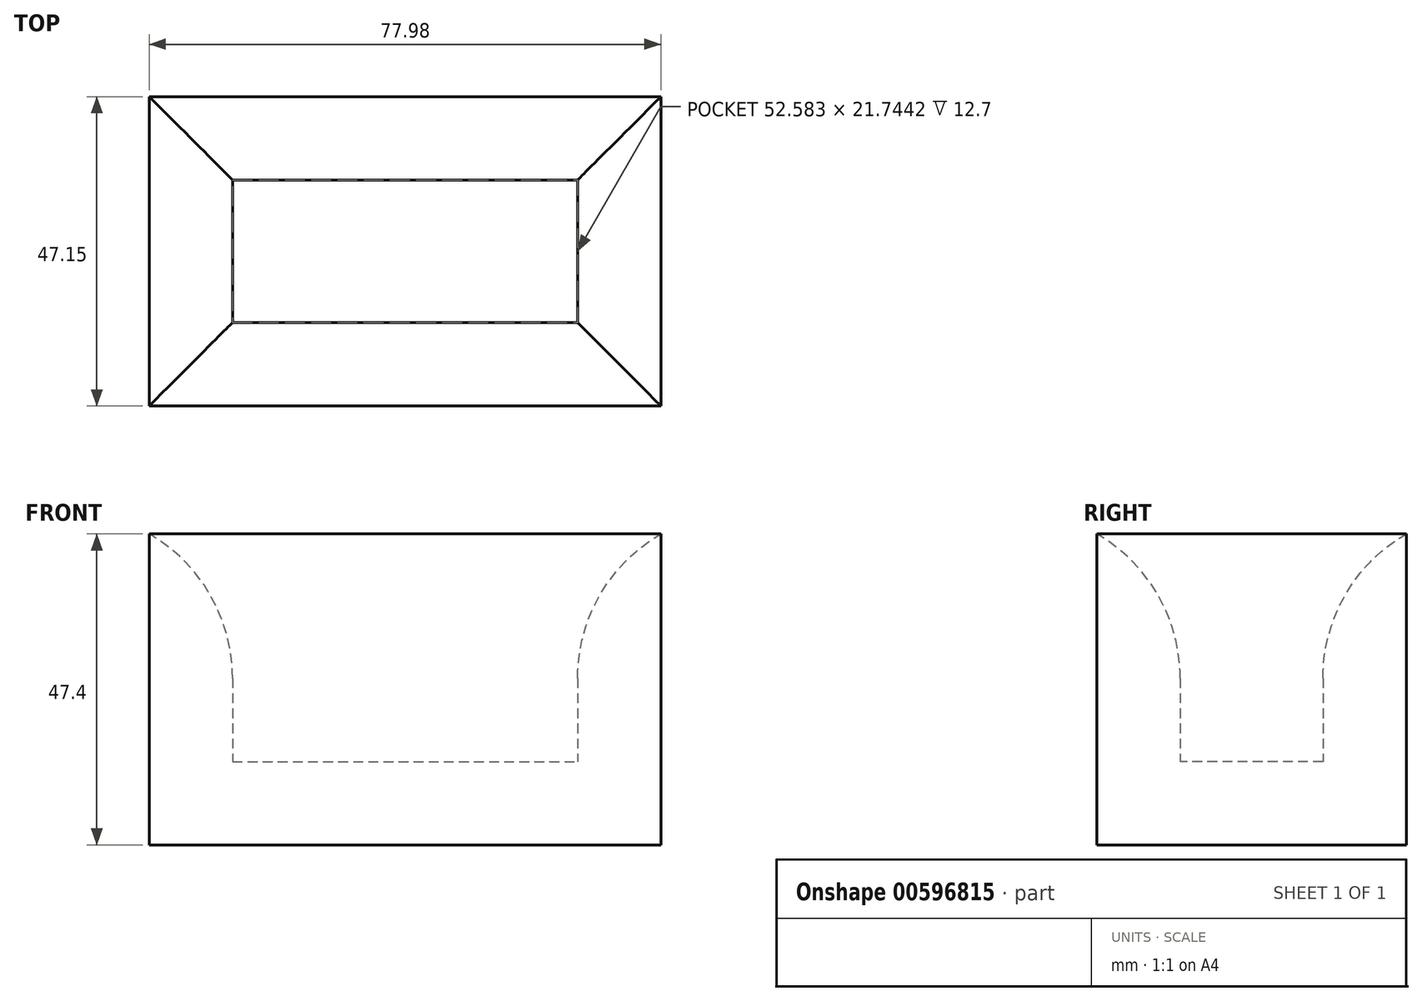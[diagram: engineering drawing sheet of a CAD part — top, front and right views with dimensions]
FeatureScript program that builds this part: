
annotation { "Feature Type Name" : "Feature", "Feature Type Description" : "" }
export const myFeature = defineFeature(function(context is Context, id is Id, definition is map)
    precondition{}
    {
        {
            var Q0;
            Q0=qCreatedBy(makeId("Top.planeOp"),FACE);
            var sketch = newSketch(context, id + "F0", { "sketchPlane" : qUnion([Q0])});
            skLineSegment(sketch, "E0.bottom", {"start": v(-13, 23.46) * mm, "end": v(64.98, 23.46) * mm});
            skLineSegment(sketch, "E0.top", {"start": v(-13, -23.69) * mm, "end": v(64.98, -23.69) * mm});
            skLineSegment(sketch, "E0.left", {"start": v(-13, 23.46) * mm, "end": v(-13, -23.69) * mm});
            skLineSegment(sketch, "E0.right", {"start": v(64.98, 23.46) * mm, "end": v(64.98, -23.69) * mm});
            skSolve(sketch);
        }
        {
            var Q0;
            Q0 = qSketchRegion(id + "F0", true);
            extrude(context, id + "F1", {"entities" : qUnion([Q0]), "depth" : 50.8 * mm, "offsetDistance" : 25.4 * mm});
        }
        {
            var Q0;
            Q0=makeQuery(id+"F1.opExtrude","CAP_FACE",FACE,{"disambiguationData":[OSD([sQuery(id+"F0.wireOp",EDGE,"E0.bottom"),sQuery(id+"F0.wireOp",EDGE,"E0.top"),sQuery(id+"F0.wireOp",EDGE,"E0.left"),sQuery(id+"F0.wireOp",EDGE,"E0.right")])],"isStart":false});
            shell(context, id + "F2", {"entities" : qUnion([Q0]), "thickness" : 12.7 * mm});
        }
        {
            var Q0;
            {var subQ0=sQuery(id+"F0.wireOp",EDGE,"E0.bottom");Q0=makeQuery(id+"F2.opShell","OFFSET_EDGE",EDGE,{"disambiguationData":[OSD([subQ0]),TDD([makeQuery(id+"F1.opExtrude","CAP_EDGE",EDGE,{"disambiguationData":[OSD([subQ0])],"isStart":false})])]});}
            var Q1;
            {var subQ0=sQuery(id+"F0.wireOp",EDGE,"E0.left");Q1=makeQuery(id+"F2.opShell","OFFSET_EDGE",EDGE,{"disambiguationData":[OSD([subQ0]),TDD([makeQuery(id+"F1.opExtrude","CAP_EDGE",EDGE,{"disambiguationData":[OSD([subQ0])],"isStart":false})])]});}
            var Q2;
            {var subQ0=sQuery(id+"F0.wireOp",EDGE,"E0.top");Q2=makeQuery(id+"F2.opShell","OFFSET_EDGE",EDGE,{"disambiguationData":[OSD([subQ0]),TDD([makeQuery(id+"F1.opExtrude","CAP_EDGE",EDGE,{"disambiguationData":[OSD([subQ0])],"isStart":false})])]});}
            var Q3;
            {var subQ0=sQuery(id+"F0.wireOp",EDGE,"E0.right");Q3=makeQuery(id+"F2.opShell","OFFSET_EDGE",EDGE,{"disambiguationData":[OSD([subQ0]),TDD([makeQuery(id+"F1.opExtrude","CAP_EDGE",EDGE,{"disambiguationData":[OSD([subQ0])],"isStart":false})])]});}
            fillet(context, id + "F3", {"entities" : qUnion([Q0, Q1, Q2, Q3]), "radius" : 25.4 * mm, "tangentPropagation" : true, "allowEdgeOverflow" : false});
        }
    });
